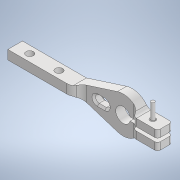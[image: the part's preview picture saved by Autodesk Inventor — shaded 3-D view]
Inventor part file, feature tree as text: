
AUTODESK INVENTOR PART (.ipt)
format: ipt  version: 2020 (Build 240168000, 168)  size: 294,912 bytes
history: native  units: mm
features: extrude x10, sketch x10, projected_geometry x8, fillet x6, other x4, chamfer x1, reference x1
ambient origin geometry x8: Origin, YZ Plane, XZ Plane, XY Plane, X Axis, Y Axis, Z Axis, Center Point
bodies: Solid1 (feature_tree)
feature tree (40):
  extrude  "Extrusion1"  Depth=8.0mm
  extrude  "Extrusion2"  Depth=2.5mm
  extrude  "Extrusion3"  Depth=5.0mm
  extrude  "Extrusion4"  Depth=5.0mm
  extrude  "Extrusion5"  Depth=2.0mm
  extrude  "Extrusion6"  Depth=4.0mm
  fillet  "Fillet1"  Radius=4.0mm
  extrude  "Extrusion7"  Depth=4.0mm
  fillet  "Fillet2"  Radius=5.0mm
  fillet  "Fillet3"  Radius=8.0mm
  fillet  "Fillet4"  Radius=4.0mm
  fillet  "Fillet5"  Radius=4.0mm
  extrude  "Extrusion8"  Depth=10.0mm TaperAngle=0.0deg
  extrude  "Extrusion9"  Depth=5.0mm
  fillet  "Fillet6"  Radius=8.0mm
  chamfer  "Chamfer1"  Distance=5.0mm
  extrude  "Extrusion10"  Depth=1.5mm
  sketch  "Sketch1"  dims[d0=8.0mm d1=60.0mm]
  reference  "Reference1"
  sketch  "Sketch2"  dims[d2=20.0mm d3=2.5mm]
  projected_geometry  "Projected Loop1"
  sketch  "Sketch3"  dims[d4=35.0mm d5=5.0mm]
  projected_geometry  "Projected Loop2"
  sketch  "Sketch4"  dims[d6=5.0mm d7=0.0mm d8=7.6mm]
  projected_geometry  "Projected Loop3"
  sketch  "Sketch5"  dims[d9=2.0mm d10=12.0mm]
  projected_geometry  "Projected Loop4"
  sketch  "Sketch6"  dims[d11=5.0mm d12=0.0mm d13=18.0mm d14=4.0mm]
  projected_geometry  "Projected Loop5"
  sketch  "Sketch7"  dims[d15=18.0mm d16=4.0mm d17=5.0mm d18=0.0mm d19=8.0mm d20=4.0mm d21=0.0mm d22=4.0mm d23=0.0mm]
  projected_geometry  "Projected Loop6"
  sketch  "Sketch8"  dims[d24=3.0mm d25=10.0mm d26=0.0mm]
  projected_geometry  "Projected Loop7"
  sketch  "Sketch9"  dims[d27=3.0mm d28=35.0mm d29=8.0mm d30=5.0mm d31=0.0mm]
  projected_geometry  "Projected Loop8"
  sketch  "Sketch10"  dims[d32=6.0mm d33=1.5mm d34=3.0mm d35=2.0mm d36=12.0mm d37=2.0mm d38=4.0mm d39=5.0mm d40=0.0mm d41=8.0mm d42=16.0mm d43=4.0mm d44=4.0mm d45=5.0mm d46=0.0mm d47=6.0mm d48=1.0mm d49=2.0mm d50=45.0deg d51=2.0mm d52=8.5mm d53=0.0mm]
  parser-record x1  (decoder bookkeeping rows leaked as tree rows — omitted from the tree; the rows remain in map.json)
  other  "delta_1.iam"
  other  "arm_shift_1:3"
  other  "pin_8_45:1"
note: 1 file-system path scrubbed to <path> (originals preserved in map.json)
